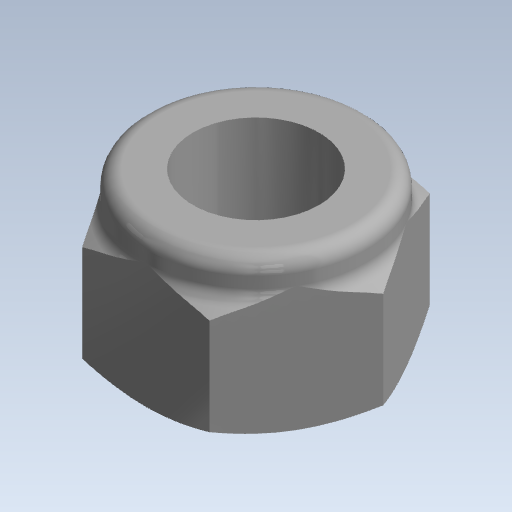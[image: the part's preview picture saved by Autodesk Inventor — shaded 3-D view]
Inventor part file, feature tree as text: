
AUTODESK INVENTOR PART (.ipt)
format: ipt  version: 2020 (Build 240168000, 168)  size: 136,704 bytes
history: native  units: mm (DEFAULTED — no unit token found)
features: fillet x1
ambient origin geometry x8: Origin, YZ Plane, XZ Plane, XY Plane, X Axis, Y Axis, Z Axis, Center Point
bodies: Solid1 (feature_tree)
feature tree (1):
  fillet  "Fillet7"  [1 undecoded]
note: 1 required parameter value undecoded (feature->parameter linkage not recoverable at this tier; creation-order binding heuristic only, values carry confidence <= 0.55)
